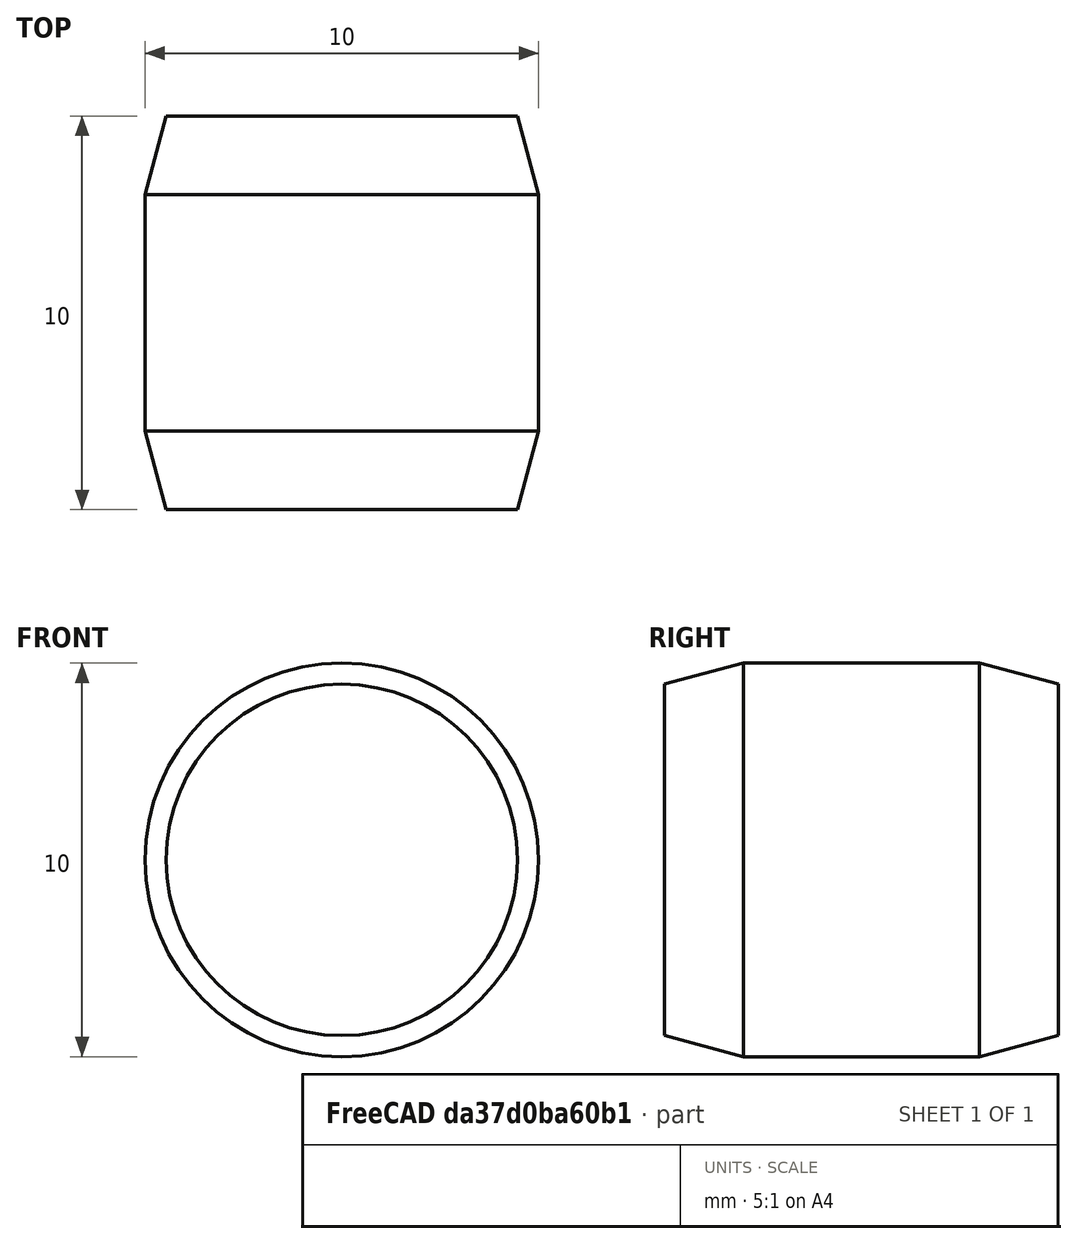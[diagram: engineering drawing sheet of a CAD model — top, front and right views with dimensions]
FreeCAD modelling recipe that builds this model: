
FCSTD DOCUMENT  (FreeCAD 0.15R4470 (Git))
Label: Zyl-Stift_ISO_8734-10x10
License: CC-BY 3.0
LicenseURL: http://creativecommons.org/licenses/by/3.0/
objects: Sketcher::SketchObject×1, PartDesign::Revolution×1
note: 3 computed .brp shape members not serialized (recipe doc carries the construction recipe); baked Part::Feature solids carry a one-line shape summary decoded from their .brp

FEATURE [Sketcher::SketchObject] Sketch
  Placement = pos=(0,0,0) rot=(0.57735,0.57735,0.57735;2.0944rad)
  sketch-geometry (7):
    g0: LineSegment StartX=0 StartY=0 StartZ=0 EndX=0 EndY=4.4641 EndZ=0
    g1: LineSegment StartX=0 StartY=4.4641 StartZ=0 EndX=2 EndY=5 EndZ=0
    g2: LineSegment StartX=2 StartY=5 StartZ=0 EndX=8 EndY=5 EndZ=0
    g3: LineSegment StartX=8 StartY=5 StartZ=0 EndX=10 EndY=4.4641 EndZ=0
    g4: LineSegment StartX=10 StartY=4.4641 StartZ=0 EndX=10 EndY=0 EndZ=0
    g5: LineSegment StartX=10 StartY=0 StartZ=0 EndX=0 EndY=0 EndZ=0
    g6: LineSegment [constr] StartX=0 StartY=4.4641 StartZ=0 EndX=10 EndY=4.4641 EndZ=0
  constraints (19):
    c: Coincident(g0,g-1)
    c: PointOnObject(g0,g-2)
    c: Coincident(g0,g1)
    c: Coincident(g1,g2)
    c: Horizontal(g2)
    c: Coincident(g2,g3)
    c: Coincident(g3,g4)
    c: Vertical(g4)
    c: Coincident(g4,g5)
    c: Coincident(g5,g-1)
    c: Horizontal(g5)
    c: Equal(g3,g1)
    c: Coincident(g6,g0)
    c: Coincident(g6,g3)
    c: Horizontal(g6)
    c: Angle(g6,g1) = 0.261799
    c: DistanceY(g-1,g1) = 5
    c: DistanceX(g5) = -10
    c: DistanceX(g1) = 2
FEATURE [PartDesign::Revolution] Revolution  label="Zyl-Stift ISO 8734-10x10 #"
  Angle = 360
  Axis = (0,1,0)
  Base = (0,0,0)
  Placement = pos=(0,0,0) rot=(0.57735,0.57735,0.57735;2.0944rad)
  ReferenceAxis = -> Sketch [H_Axis]
  Sketch = -> Sketch
